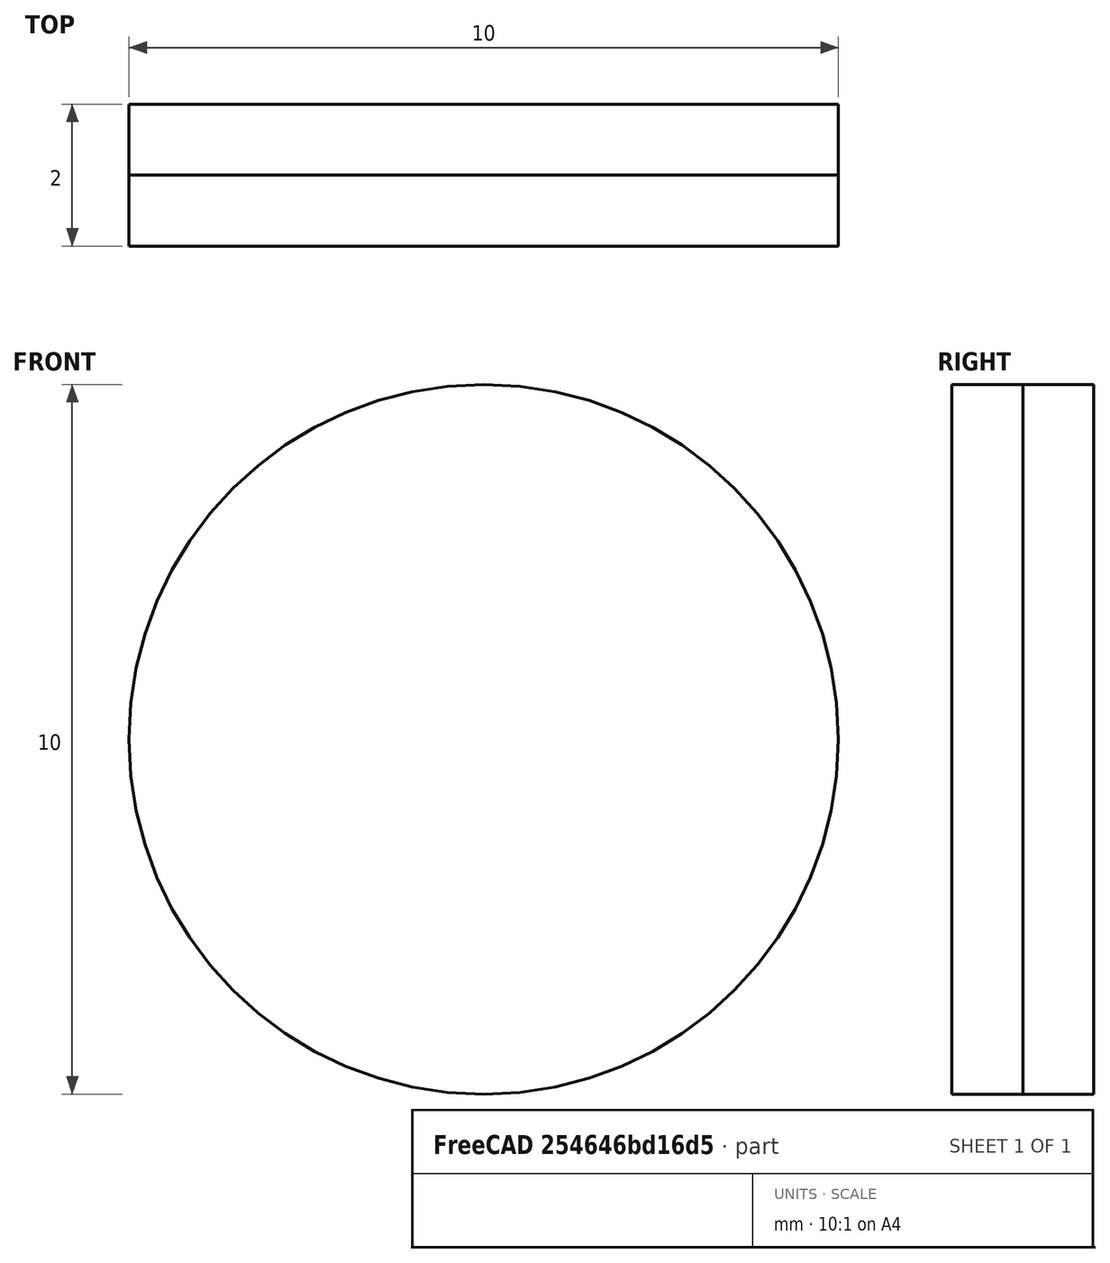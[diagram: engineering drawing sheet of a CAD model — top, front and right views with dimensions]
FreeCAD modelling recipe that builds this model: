
FCSTD DOCUMENT  (FreeCAD 0.21R33771 (Git))
Label: Magnet
License: Public Domain
LicenseURL: https://en.wikipedia.org/wiki/Public_domain
objects: App::Part×3, Part::Cylinder×2, PartDesign::CoordinateSystem×1
note: 3 computed .brp shape members not serialized (recipe doc carries the construction recipe); baked Part::Feature solids carry a one-line shape summary decoded from their .brp

FEATURE [Part::Cylinder] Cylinder  label="SouthMagPole"
  Angle = 360
  AttacherType = Attacher::AttachEngine3D
  FirstAngle = 0
  Height = 1
  Placement = pos=(0,0,0) rot=(1,0,0;1.5708rad)
  Radius = 5
  SecondAngle = 0
FEATURE [App::Part] Part001  label="South Pole"
  Group = -> [Cylinder]
  Origin = -> Origin001
FEATURE [Part::Cylinder] Cylinder001  label="NorthMagPole"
  Angle = 360
  AttacherType = Attacher::AttachEngine3D
  FirstAngle = 0
  Height = 1
  Placement = pos=(0,-1,2e-16) rot=(1,0,0;1.5708rad)
  Radius = 5
  SecondAngle = 0
FEATURE [App::Part] Part002  label="North Pole"
  Group = -> [Cylinder001]
  Origin = -> Origin002
FEATURE [PartDesign::CoordinateSystem] AP  label="Magnet AP"
  AttacherType = Attacher::AttachEngine3D
  AttachmentOffset = pos=(0,0,0) rot=(-0.57735,0.57735,-0.57735;2.0944rad)
  MapMode = 11
  Placement = pos=(0,-2,0) rot=(0,0,1;0rad)
  Support = -> [Cylinder001]
FEATURE [App::Part] Part  label="Magnet"
  Group = -> [Part001,Part002,AP]
  Origin = -> Origin
  Placement = pos=(-8e-16,-2,0) rot=(0,0,1;3.14159rad)
